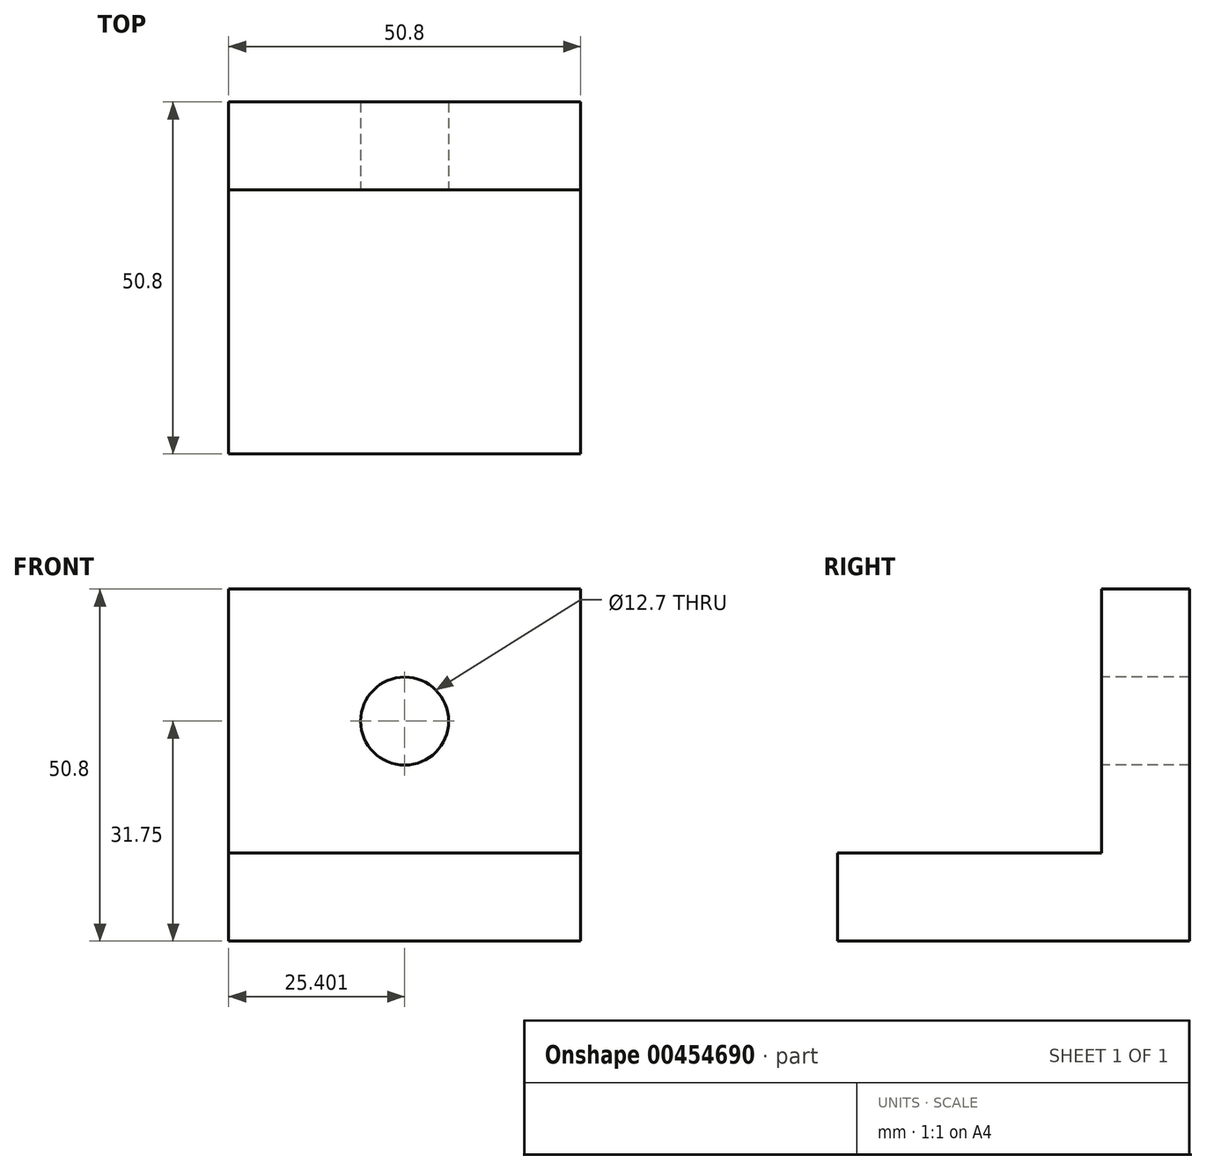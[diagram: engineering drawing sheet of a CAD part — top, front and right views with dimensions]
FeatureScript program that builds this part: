
annotation { "Feature Type Name" : "Feature", "Feature Type Description" : "" }
export const myFeature = defineFeature(function(context is Context, id is Id, definition is map)
    precondition{}
    {
        {
            var Q0;
            Q0=qCreatedBy(makeId("Top.planeOp"),FACE);
            var sketch = newSketch(context, id + "F0", { "sketchPlane" : qUnion([Q0])});
            skLineSegment(sketch, "E0.bottom", {"start": v(-10.32, 8.32) * mm, "end": v(-61.12, 8.32) * mm});
            skLineSegment(sketch, "E0.top", {"start": v(-10.32, 59.12) * mm, "end": v(-61.12, 59.12) * mm});
            skLineSegment(sketch, "E0.left", {"start": v(-10.32, 8.32) * mm, "end": v(-10.32, 59.12) * mm});
            skLineSegment(sketch, "E0.right", {"start": v(-61.12, 8.32) * mm, "end": v(-61.12, 59.12) * mm});
            skSolve(sketch);
        }
        {
            var Q0;
            Q0=makeQuery(id+"F0.imprint","IMPRINT",FACE,{"disambiguationData":[TD([[makeQuery(id+"F0.imprint","IMPRINT",EDGE,{"derivedFrom":sQuery(id+"F0.wireOp",EDGE,"E0.bottom")}),-1.0]])]});
            extrude(context, id + "F1", {"entities" : qUnion([Q0]), "depth" : 12.7 * mm});
        }
        {
            var Q0;
            Q0=makeQuery(id+"F1.opExtrude","CAP_FACE",FACE,{"disambiguationData":[OSD([sQuery(id+"F0.wireOp",EDGE,"E0.bottom"),sQuery(id+"F0.wireOp",EDGE,"E0.top"),sQuery(id+"F0.wireOp",EDGE,"E0.left"),sQuery(id+"F0.wireOp",EDGE,"E0.right")])],"isStart":false});
            var sketch = newSketch(context, id + "F2", { "sketchPlane" : qUnion([Q0])});
            skLineSegment(sketch, "E1.bottom", {"start": v(-61.12, 59.12) * mm, "end": v(-10.32, 59.12) * mm});
            skLineSegment(sketch, "E1.top", {"start": v(-61.12, 46.42) * mm, "end": v(-10.32, 46.42) * mm});
            skLineSegment(sketch, "E1.left", {"start": v(-61.12, 59.12) * mm, "end": v(-61.12, 46.42) * mm});
            skLineSegment(sketch, "E1.right", {"start": v(-10.32, 59.12) * mm, "end": v(-10.32, 46.42) * mm});
            skSolve(sketch);
        }
        {
            var Q0;
            Q0=makeQuery(id+"F2.imprint","IMPRINT",FACE,{"disambiguationData":[TD([[makeQuery(id+"F2.imprint","IMPRINT",EDGE,{"derivedFrom":sQuery(id+"F2.wireOp",EDGE,"E1.bottom")}),1.0]])]});
            extrude(context, id + "F3", {"entities" : qUnion([Q0]), "operationType" : NewBodyOperationType.ADD, "depth" : 38.1 * mm});
        }
        {
            var Q0;
            Q0=makeQuery(id+"F3.opExtrude","SWEPT_FACE",FACE,{"disambiguationData":[OSD([sQuery(id+"F2.wireOp",EDGE,"E1.top")])]});
            var sketch = newSketch(context, id + "F4", { "sketchPlane" : qUnion([Q0])});
            skCircle(sketch, "E2", {"center": v(-35.72, 31.75) * mm, "radius": 6.35 * mm});
            skSolve(sketch);
        }
        {
            var Q0;
            Q0=makeQuery(id+"F4.imprint","IMPRINT",FACE,{"disambiguationData":[TD([[makeQuery(id+"F4.imprint","IMPRINT",EDGE,{"derivedFrom":sQuery(id+"F4.wireOp",EDGE,"E2")}),1.0]])]});
            extrude(context, id + "F5", {"entities" : qUnion([Q0]), "operationType" : NewBodyOperationType.REMOVE, "endBound" : BoundingType.THROUGH_ALL, "oppositeDirection" : true, "depth" : 25.4 * mm});
        }
    });
